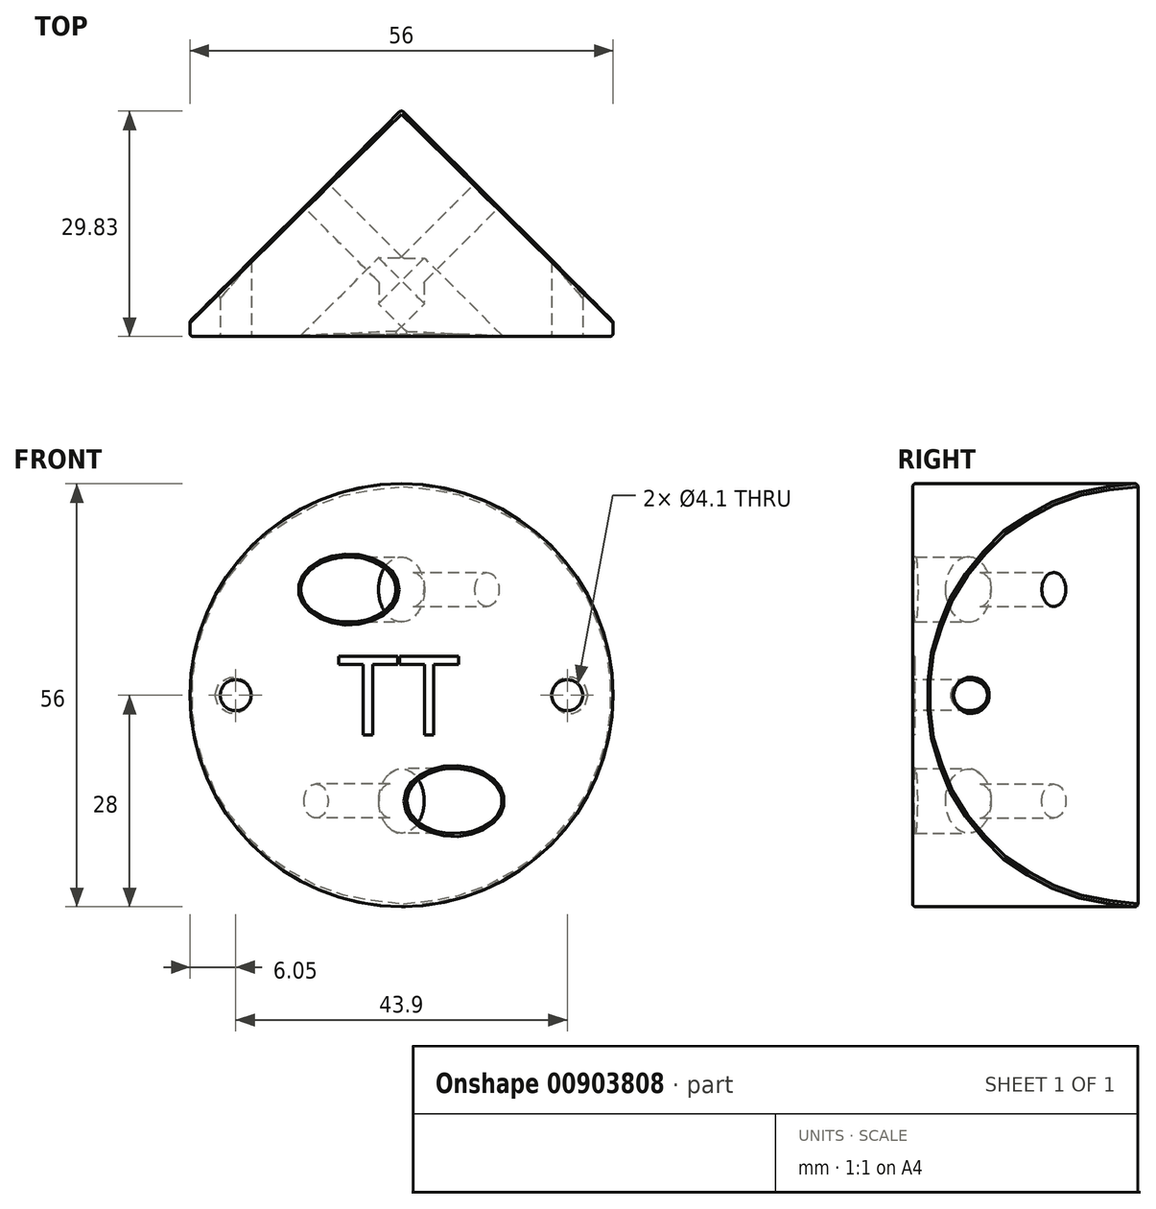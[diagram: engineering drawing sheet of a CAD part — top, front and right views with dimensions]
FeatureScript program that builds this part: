
annotation { "Feature Type Name" : "Feature", "Feature Type Description" : "" }
export const myFeature = defineFeature(function(context is Context, id is Id, definition is map)
    precondition{}
    {
        {
            var Q0;
            Q0=qCreatedBy(makeId("Front.planeOp"),FACE);
            var sketch = newSketch(context, id + "F0", { "sketchPlane" : qUnion([Q0])});
            skCircle(sketch, "E0", {"center": v(0, 0) * mm, "radius": 28 * mm});
            skSolve(sketch);
        }
        {
            var Q0;
            Q0 = qSketchRegion(id + "F0", true);
            extrude(context, id + "F1", {"entities" : qUnion([Q0]), "depth" : 80 * mm, "offsetDistance" : 25 * mm});
        }
        {
            var Q0;
            Q0=qCreatedBy(makeId("Top.planeOp"),FACE);
            var sketch = newSketch(context, id + "F2", { "sketchPlane" : qUnion([Q0])});
            skLineSegment(sketch, "E1", {"start": v(0, -50) * mm, "end": v(-28.67, -78.67) * mm});
            skLineSegment(sketch, "E2", {"start": v(0, -50) * mm, "end": v(28.67, -78.67) * mm});
            skLineSegment(sketch, "E3", {"start": v(-28.67, -78.67) * mm, "end": v(-55.6, 39.79) * mm});
            skLineSegment(sketch, "E4", {"start": v(-55.6, 39.79) * mm, "end": v(113.17, 16.85) * mm});
            skLineSegment(sketch, "E5", {"start": v(113.17, 16.85) * mm, "end": v(28.67, -78.67) * mm});
            skSolve(sketch);
        }
        {
            var Q0;
            Q0=makeQuery(id+"F2.imprint","IMPRINT",FACE,{"disambiguationData":[TD([[makeQuery(id+"F2.imprint","IMPRINT",EDGE,{"derivedFrom":sQuery(id+"F2.wireOp",EDGE,"E1")}),-1.0]])]});
            extrude(context, id + "F3", {"entities" : qUnion([Q0]), "operationType" : NewBodyOperationType.REMOVE, "endBound" : BoundingType.SYMMETRIC, "oppositeDirection" : true, "depth" : 80 * mm, "offsetDistance" : 25 * mm});
        }
        {
            var Q0;
            Q0=makeQuery(id+"F3.boolean.opBoolean","COPY",FACE,{"derivedFrom":makeQuery(id+"F3.opExtrude","SWEPT_FACE",FACE,{"disambiguationData":[OSD([sQuery(id+"F2.wireOp",EDGE,"E1")])]})});
            var sketch = newSketch(context, id + "F4", { "sketchPlane" : qUnion([Q0])});
            skCircle(sketch, "E6", {"center": v(51.36, -14) * mm, "radius": 2.25 * mm});
            skLineSegment(sketch, "E7", {"start": v(35.36, 0) * mm, "end": v(35.36, -28) * mm, "construction": true});
            skPoint(sketch, "E8", {"position": v(35.36, -14) * mm});
            skSolve(sketch);
        }
        {
            var Q0;
            Q0 = qSketchRegion(id + "F4", true);
            extrude(context, id + "F5", {"entities" : qUnion([Q0]), "operationType" : NewBodyOperationType.REMOVE, "endBound" : BoundingType.THROUGH_ALL, "oppositeDirection" : true, "depth" : 25 * mm, "offsetDistance" : 25 * mm});
        }
        {
            var Q0;
            Q0=makeQuery(id+"F3.boolean.opBoolean","COPY",FACE,{"derivedFrom":makeQuery(id+"F3.opExtrude","SWEPT_FACE",FACE,{"disambiguationData":[OSD([sQuery(id+"F2.wireOp",EDGE,"E1")])]})});
            cPlane(context, id + "F6", {"entities" : qUnion([Q0]), "cplaneType" : CPlaneType.OFFSET, "offset" : 16 * mm, "oppositeDirection" : true, "width" : 150 * mm, "height" : 150 * mm});
        }
        {
            var Q0;
            Q0=qCreatedBy(id+"F6.planeOp",FACE);
            var sketch = newSketch(context, id + "F7", { "sketchPlane" : qUnion([Q0])});
            skCircle(sketch, "E9", {"center": v(51.36, -14) * mm, "radius": 4.3 * mm});
            skSolve(sketch);
        }
        {
            var Q0;
            Q0 = qSketchRegion(id + "F7", true);
            extrude(context, id + "F8", {"entities" : qUnion([Q0]), "operationType" : NewBodyOperationType.REMOVE, "oppositeDirection" : true, "depth" : 25 * mm, "offsetDistance" : 25 * mm});
        }
        {
            var Q0;
            Q0=makeQuery(id+"F8.boolean.opBoolean","INTERSECT",EDGE,{"derivedFrom":[makeQuery(id+"F5.boolean.opBoolean","COPY",FACE,{"derivedFrom":makeQuery(id+"F5.opExtrude","SWEPT_FACE",FACE,{"disambiguationData":[OSD([sQuery(id+"F4.wireOp",EDGE,"E6")])]})}),makeQuery(id+"F8.opExtrude","CAP_FACE",FACE,{"disambiguationData":[OSD([sQuery(id+"F7.wireOp",EDGE,"E9")])],"isStart":true})]});
            chamfer(context, id + "F9", {"entities" : qUnion([Q0]), "chamferType" : ChamferType.OFFSET_ANGLE, "width" : 2 * mm, "oppositeDirection" : false, "angle" : 45 * degree, "tangentPropagation" : true});
        }
        {
            var Q0;
            Q0=makeQuery(id+"F3.boolean.opBoolean","COPY",FACE,{"derivedFrom":makeQuery(id+"F3.opExtrude","SWEPT_FACE",FACE,{"disambiguationData":[OSD([sQuery(id+"F2.wireOp",EDGE,"E2")])]})});
            var sketch = newSketch(context, id + "F10", { "sketchPlane" : qUnion([Q0])});
            skCircle(sketch, "E10", {"center": v(-51.36, 14) * mm, "radius": 2.25 * mm});
            skLineSegment(sketch, "E11", {"start": v(-35.36, 28) * mm, "end": v(-35.36, 0) * mm, "construction": true});
            skPoint(sketch, "E12", {"position": v(-35.36, 14) * mm});
            skSolve(sketch);
        }
        {
            var Q0;
            Q0 = qSketchRegion(id + "F10", true);
            extrude(context, id + "F11", {"entities" : qUnion([Q0]), "operationType" : NewBodyOperationType.REMOVE, "endBound" : BoundingType.THROUGH_ALL, "oppositeDirection" : true, "depth" : 25 * mm, "offsetDistance" : 25 * mm});
        }
        {
            var Q0;
            Q0=makeQuery(id+"F3.boolean.opBoolean","COPY",FACE,{"derivedFrom":makeQuery(id+"F3.opExtrude","SWEPT_FACE",FACE,{"disambiguationData":[OSD([sQuery(id+"F2.wireOp",EDGE,"E2")])]})});
            cPlane(context, id + "F12", {"entities" : qUnion([Q0]), "cplaneType" : CPlaneType.OFFSET, "offset" : 16 * mm, "oppositeDirection" : true, "width" : 150 * mm, "height" : 150 * mm});
        }
        {
            var Q0;
            Q0=qCreatedBy(id+"F12.planeOp",FACE);
            var sketch = newSketch(context, id + "F13", { "sketchPlane" : qUnion([Q0])});
            skCircle(sketch, "E13", {"center": v(-51.36, 14) * mm, "radius": 4.3 * mm});
            skSolve(sketch);
        }
        {
            var Q0;
            Q0 = qSketchRegion(id + "F13", true);
            extrude(context, id + "F14", {"entities" : qUnion([Q0]), "operationType" : NewBodyOperationType.REMOVE, "endBound" : BoundingType.THROUGH_ALL, "oppositeDirection" : true, "depth" : 25 * mm, "offsetDistance" : 25 * mm});
        }
        {
            var Q0;
            Q0=makeQuery(id+"F14.boolean.opBoolean","INTERSECT",EDGE,{"derivedFrom":[makeQuery(id+"F11.boolean.opBoolean","COPY",FACE,{"derivedFrom":makeQuery(id+"F11.opExtrude","SWEPT_FACE",FACE,{"disambiguationData":[OSD([sQuery(id+"F10.wireOp",EDGE,"E10")])]})}),makeQuery(id+"F14.opExtrude","CAP_FACE",FACE,{"disambiguationData":[OSD([sQuery(id+"F13.wireOp",EDGE,"E13")])],"isStart":true})]});
            chamfer(context, id + "F15", {"entities" : qUnion([Q0]), "chamferType" : ChamferType.OFFSET_ANGLE, "width" : 2 * mm, "oppositeDirection" : false, "angle" : 45 * degree, "tangentPropagation" : true});
        }
        {
            var Q0;
            Q0=makeQuery(id+"F1.opExtrude","CAP_FACE",FACE,{"disambiguationData":[OSD([sQuery(id+"F0.wireOp",EDGE,"E0")])],"isStart":false});
            var sketch = newSketch(context, id + "F16", { "sketchPlane" : qUnion([Q0])});
            skLineSegment(sketch, "E14", {"start": v(28, 0) * mm, "end": v(-28, 0) * mm, "construction": true});
            skCircle(sketch, "E15", {"center": v(21.95, 0) * mm, "radius": 2.05 * mm});
            skCircle(sketch, "E16", {"center": v(-21.95, 0) * mm, "radius": 2.05 * mm});
            skLineSegment(sketch, "E17", {"start": v(0, 0) * mm, "end": v(0, -6.47) * mm, "construction": true});
            skSolve(sketch);
        }
        {
            var Q0;
            Q0 = qSketchRegion(id + "F16", true);
            extrude(context, id + "F17", {"entities" : qUnion([Q0]), "operationType" : NewBodyOperationType.REMOVE, "oppositeDirection" : true, "depth" : 25 * mm, "offsetDistance" : 25 * mm});
        }
        {
            var Q0;
            Q0=makeQuery(id+"F1.opExtrude","CAP_FACE",FACE,{"disambiguationData":[OSD([sQuery(id+"F0.wireOp",EDGE,"E0")])],"isStart":false});
            var Q1;
            Q1=makeQuery(id+"F5.boolean.opBoolean","COPY",EDGE,{"derivedFrom":makeQuery(id+"F5.opExtrude","CAP_EDGE",EDGE,{"disambiguationData":[OSD([sQuery(id+"F4.wireOp",EDGE,"E6")])],"isStart":true})});
            var Q2;
            {var subQ0=makeQuery(id+"F11.boolean.opBoolean","COPY",FACE,{"derivedFrom":makeQuery(id+"F11.opExtrude","SWEPT_FACE",FACE,{"disambiguationData":[OSD([sQuery(id+"F10.wireOp",EDGE,"E10")])]})});Q2=makeQuery(id+"F15.opChamfer","BLEND_EDGE",EDGE,{"blendedFrom":[makeQuery(id+"F14.boolean.opBoolean","INTERSECT",EDGE,{"derivedFrom":[subQ0,makeQuery(id+"F14.opExtrude","CAP_FACE",FACE,{"disambiguationData":[OSD([sQuery(id+"F13.wireOp",EDGE,"E13")])],"isStart":true})]}),subQ0],"blendedInto":[subQ0]});}
            var Q3;
            Q3=makeQuery(id+"F17.boolean.opBoolean","COPY",EDGE,{"derivedFrom":makeQuery(id+"F17.opExtrude","CAP_EDGE",EDGE,{"disambiguationData":[OSD([sQuery(id+"F16.wireOp",EDGE,"E16")])],"isStart":true})});
            var Q4;
            Q4=makeQuery(id+"F14.boolean.opBoolean","INTERSECT",EDGE,{"derivedFrom":[makeQuery(id+"F1.opExtrude","CAP_FACE",FACE,{"disambiguationData":[OSD([sQuery(id+"F0.wireOp",EDGE,"E0")])],"isStart":false}),makeQuery(id+"F14.opExtrude","SWEPT_FACE",FACE,{"disambiguationData":[OSD([sQuery(id+"F13.wireOp",EDGE,"E13")])]})]});
            var Q5;
            {var subQ0=makeQuery(id+"F5.boolean.opBoolean","COPY",FACE,{"derivedFrom":makeQuery(id+"F5.opExtrude","SWEPT_FACE",FACE,{"disambiguationData":[OSD([sQuery(id+"F4.wireOp",EDGE,"E6")])]})});Q5=makeQuery(id+"F9.opChamfer","BLEND_EDGE",EDGE,{"blendedFrom":[makeQuery(id+"F8.boolean.opBoolean","INTERSECT",EDGE,{"derivedFrom":[subQ0,makeQuery(id+"F8.opExtrude","CAP_FACE",FACE,{"disambiguationData":[OSD([sQuery(id+"F7.wireOp",EDGE,"E9")])],"isStart":true})]}),subQ0],"blendedInto":[subQ0]});}
            var Q6;
            Q6=makeQuery(id+"F11.boolean.opBoolean","COPY",EDGE,{"derivedFrom":makeQuery(id+"F11.opExtrude","CAP_EDGE",EDGE,{"disambiguationData":[OSD([sQuery(id+"F10.wireOp",EDGE,"E10")])],"isStart":true})});
            var Q7;
            Q7=makeQuery(id+"F8.boolean.opBoolean","INTERSECT",EDGE,{"derivedFrom":[makeQuery(id+"F1.opExtrude","CAP_FACE",FACE,{"disambiguationData":[OSD([sQuery(id+"F0.wireOp",EDGE,"E0")])],"isStart":false}),makeQuery(id+"F8.opExtrude","SWEPT_FACE",FACE,{"disambiguationData":[OSD([sQuery(id+"F7.wireOp",EDGE,"E9")])]})]});
            var Q8;
            Q8=makeQuery(id+"F8.boolean.opBoolean","COPY",EDGE,{"derivedFrom":makeQuery(id+"F8.opExtrude","CAP_EDGE",EDGE,{"disambiguationData":[OSD([sQuery(id+"F7.wireOp",EDGE,"E9")])],"isStart":true})});
            var Q9;
            Q9=makeQuery(id+"F17.boolean.opBoolean","COPY",EDGE,{"derivedFrom":makeQuery(id+"F17.opExtrude","CAP_EDGE",EDGE,{"disambiguationData":[OSD([sQuery(id+"F16.wireOp",EDGE,"E15")])],"isStart":true})});
            var Q10;
            Q10=makeQuery(id+"F17.boolean.opBoolean","INTERSECT",EDGE,{"derivedFrom":[makeQuery(id+"F3.boolean.opBoolean","COPY",FACE,{"derivedFrom":makeQuery(id+"F3.opExtrude","SWEPT_FACE",FACE,{"disambiguationData":[OSD([sQuery(id+"F2.wireOp",EDGE,"E2")])]})}),makeQuery(id+"F17.opExtrude","SWEPT_FACE",FACE,{"disambiguationData":[OSD([sQuery(id+"F16.wireOp",EDGE,"E15")])]})]});
            var Q11;
            Q11=makeQuery(id+"F17.boolean.opBoolean","INTERSECT",EDGE,{"derivedFrom":[makeQuery(id+"F3.boolean.opBoolean","COPY",FACE,{"derivedFrom":makeQuery(id+"F3.opExtrude","SWEPT_FACE",FACE,{"disambiguationData":[OSD([sQuery(id+"F2.wireOp",EDGE,"E1")])]})}),makeQuery(id+"F17.opExtrude","SWEPT_FACE",FACE,{"disambiguationData":[OSD([sQuery(id+"F16.wireOp",EDGE,"E16")])]})]});
            var Q12;
            Q12=makeQuery(id+"F1.opExtrude","CAP_EDGE",EDGE,{"disambiguationData":[OSD([sQuery(id+"F0.wireOp",EDGE,"E0")])],"isStart":false});
            var Q13;
            Q13=makeQuery(id+"F3.boolean.opBoolean","INTERSECT",EDGE,{"derivedFrom":[makeQuery(id+"F1.opExtrude","SWEPT_FACE",FACE,{"disambiguationData":[OSD([sQuery(id+"F0.wireOp",EDGE,"E0")])]}),makeQuery(id+"F3.opExtrude","SWEPT_FACE",FACE,{"disambiguationData":[OSD([sQuery(id+"F2.wireOp",EDGE,"E2")])]})]});
            var Q14;
            Q14=makeQuery(id+"F3.boolean.opBoolean","INTERSECT",EDGE,{"derivedFrom":[makeQuery(id+"F1.opExtrude","SWEPT_FACE",FACE,{"disambiguationData":[OSD([sQuery(id+"F0.wireOp",EDGE,"E0")])]}),makeQuery(id+"F3.opExtrude","SWEPT_FACE",FACE,{"disambiguationData":[OSD([sQuery(id+"F2.wireOp",EDGE,"E1")])]})]});
            var Q15;
            Q15=makeQuery(id+"F3.boolean.opBoolean","COPY",EDGE,{"derivedFrom":makeQuery(id+"F3.opExtrude","SWEPT_EDGE",EDGE,{"disambiguationData":[OSD([sQuery(id+"F2.wireOp",EDGE,"E1"),sQuery(id+"F2.wireOp",EDGE,"E2")])]})});
            var Q16;
            Q16=makeQuery(id+"F15.opChamfer","BLEND_FACE",FACE,{"disambiguationData":[OSD([sQuery(id+"F10.wireOp",EDGE,"E10"),sQuery(id+"F13.wireOp",EDGE,"E13")])]});
            var Q17;
            {var subQ0=makeQuery(id+"F14.opExtrude","CAP_FACE",FACE,{"disambiguationData":[OSD([sQuery(id+"F13.wireOp",EDGE,"E13")])],"isStart":true});Q17=makeQuery(id+"F15.opChamfer","BLEND_EDGE",EDGE,{"blendedFrom":[makeQuery(id+"F14.boolean.opBoolean","INTERSECT",EDGE,{"derivedFrom":[makeQuery(id+"F11.boolean.opBoolean","COPY",FACE,{"derivedFrom":makeQuery(id+"F11.opExtrude","SWEPT_FACE",FACE,{"disambiguationData":[OSD([sQuery(id+"F10.wireOp",EDGE,"E10")])]})}),subQ0]}),makeQuery(id+"F14.boolean.opBoolean","COPY",FACE,{"derivedFrom":subQ0})],"blendedInto":[makeQuery(id+"F14.boolean.opBoolean","COPY",FACE,{"derivedFrom":subQ0})]});}
            fillet(context, id + "F18", {"entities" : qUnion([Q0, Q1, Q2, Q3, Q4, Q5, Q6, Q7, Q8, Q9, Q10, Q11, Q12, Q13, Q14, Q15, Q16, Q17]), "radius" : .4 * mm, "tangentPropagation" : true, "allowEdgeOverflow" : false});
        }
        {
            var Q0;
            Q0=makeQuery(id+"F1.opExtrude","CAP_FACE",FACE,{"disambiguationData":[OSD([sQuery(id+"F0.wireOp",EDGE,"E0")])],"isStart":false});
            var sketch = newSketch(context, id + "F19", { "sketchPlane" : qUnion([Q0])});
            skText(sketch, "E18", { "text": "TT", "fontName": "OpenSans-Regular.ttf"});
            const initialGuessF19  = {"E18": [-0.00847, -0.00525, 1, 0, 0.0105]};
            skSetInitialGuess(sketch, initialGuessF19);
            skSolve(sketch);
        }
        {
            var Q0;
            Q0 = qSketchRegion(id + "F19", true);
            extrude(context, id + "F20", {"entities" : qUnion([Q0]), "operationType" : NewBodyOperationType.REMOVE, "oppositeDirection" : true, "depth" : .25 * mm, "offsetDistance" : 25 * mm});
        }
    });
